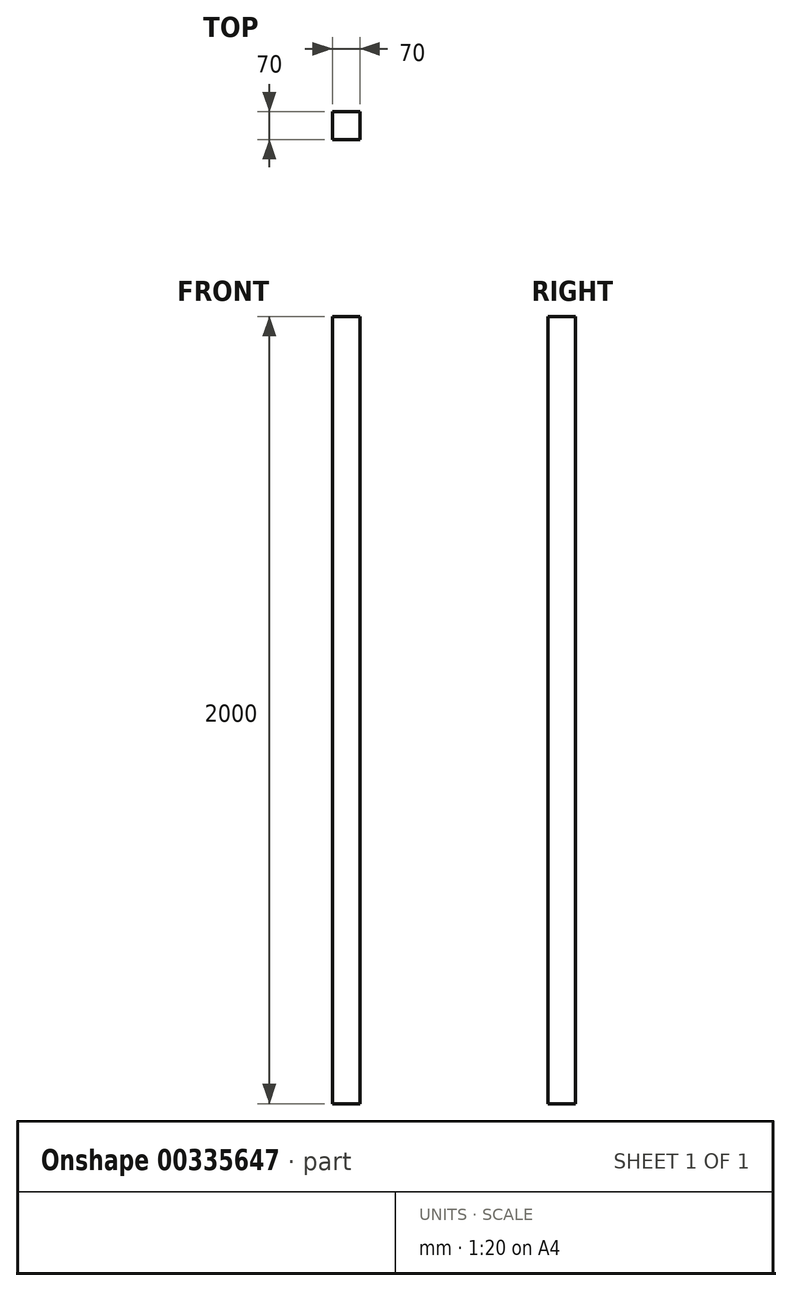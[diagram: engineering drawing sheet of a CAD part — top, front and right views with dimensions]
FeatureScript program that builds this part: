
annotation { "Feature Type Name" : "Feature", "Feature Type Description" : "" }
export const myFeature = defineFeature(function(context is Context, id is Id, definition is map)
    precondition{}
    {
        {
            var Q0;
            Q0=qCreatedBy(makeId("Top.planeOp"),FACE);
            var sketch = newSketch(context, id + "F0", { "sketchPlane" : qUnion([Q0])});
            skLineSegment(sketch, "E0.bottom", {"start": v(0, 0) * mm, "end": v(70, 0) * mm});
            skLineSegment(sketch, "E0.top", {"start": v(0, 70) * mm, "end": v(70, 70) * mm});
            skLineSegment(sketch, "E0.left", {"start": v(0, 0) * mm, "end": v(0, 70) * mm});
            skLineSegment(sketch, "E0.right", {"start": v(70, 0) * mm, "end": v(70, 70) * mm});
            skSolve(sketch);
        }
        {
            var Q0;
            Q0 = qSketchRegion(id + "F0", true);
            extrude(context, id + "F1", {"entities" : qUnion([Q0]), "depth" : 2000 * mm});
        }
    });
